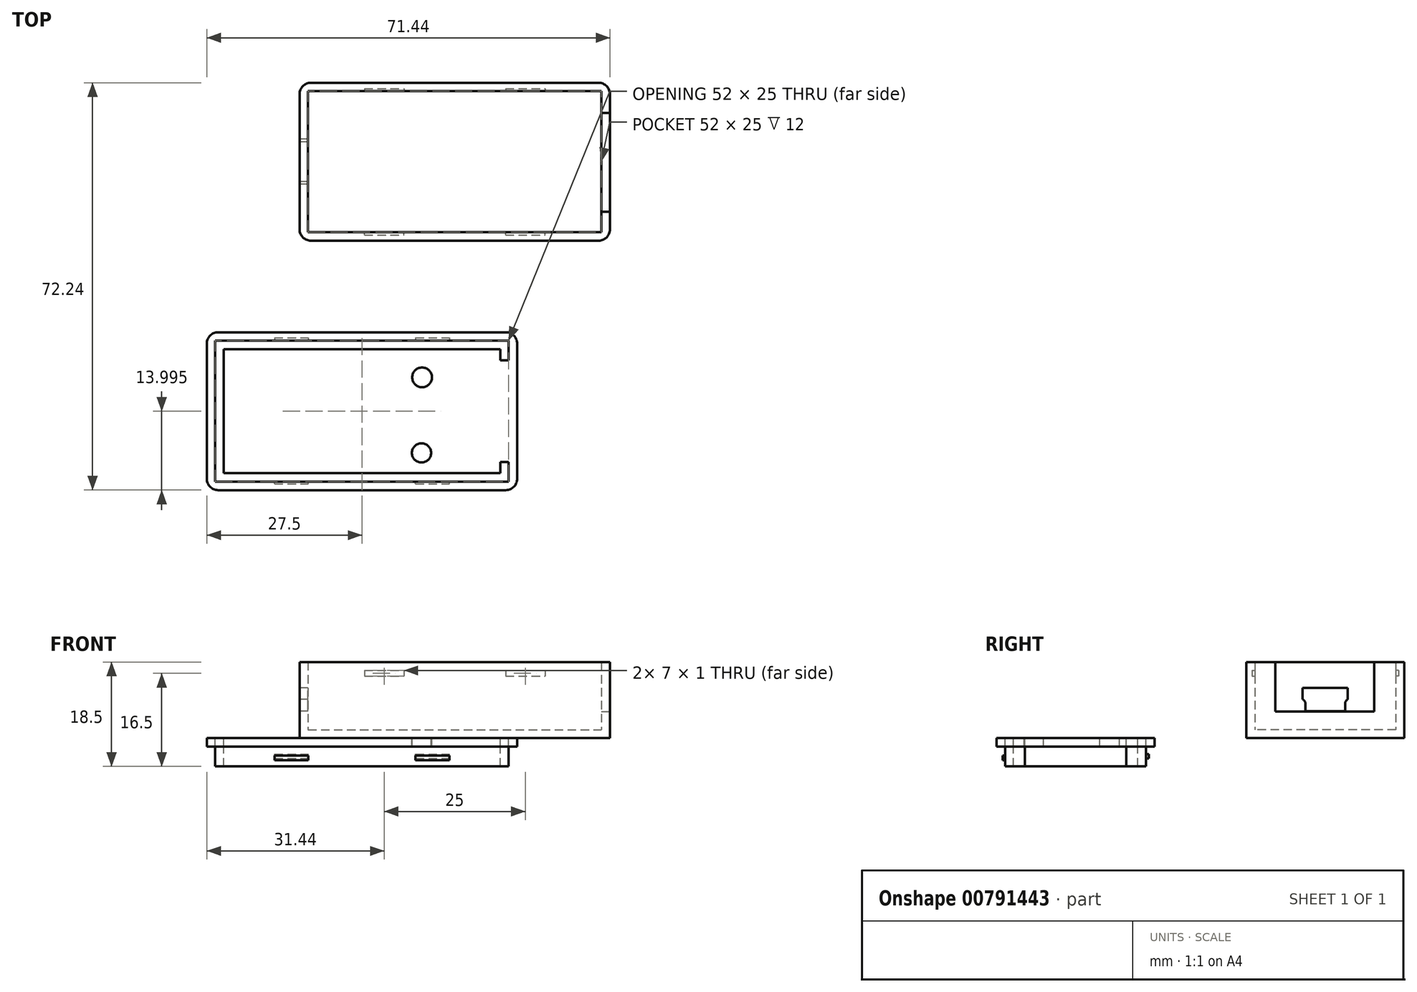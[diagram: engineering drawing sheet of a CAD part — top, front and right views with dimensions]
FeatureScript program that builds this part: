
annotation { "Feature Type Name" : "Feature", "Feature Type Description" : "" }
export const myFeature = defineFeature(function(context is Context, id is Id, definition is map)
    precondition{}
    {
        {
            var Q0;
            Q0=qCreatedBy(makeId("Top.planeOp"),FACE);
            var sketch = newSketch(context, id + "F0", { "sketchPlane" : qUnion([Q0])});
            skLineSegment(sketch, "E0.bottom", {"start": v(-26, 12.5) * mm, "end": v(26, 12.5) * mm});
            skLineSegment(sketch, "E0.top", {"start": v(-26, -12.5) * mm, "end": v(26, -12.5) * mm});
            skLineSegment(sketch, "E0.left", {"start": v(-26, 12.5) * mm, "end": v(-26, -12.5) * mm});
            skLineSegment(sketch, "E0.right", {"start": v(26, 12.5) * mm, "end": v(26, -12.5) * mm});
            skPoint(sketch, "E0.middle", {"position": v(0, 0) * mm});
            skCircle(sketch, "E1", {"center": v(-21.94, 0) * mm, "radius": 1.75 * mm});
            skLineSegment(sketch, "E2.0", {"start": v(-25.5, 14) * mm, "end": v(25.5, 14) * mm});
            skLineSegment(sketch, "E2.1", {"start": v(-27.5, 12) * mm, "end": v(-27.5, -12) * mm});
            skLineSegment(sketch, "E2.2", {"start": v(-25.5, -14) * mm, "end": v(25.5, -14) * mm});
            skLineSegment(sketch, "E2.3", {"start": v(27.5, 12) * mm, "end": v(27.5, -12) * mm});
            skPoint(sketch, "E3.visualSharp", {"position": v(27.5, 14) * mm});
            skArc(sketch, "E3.filletArc", {"start": v(27.5, 12) * mm, "mid": v(26.91, 13.41) * mm, "end": v(25.5, 14) * mm});
            skPoint(sketch, "E4.visualSharp", {"position": v(27.5, -14) * mm});
            skArc(sketch, "E4.filletArc", {"start": v(25.5, -14) * mm, "mid": v(26.91, -13.41) * mm, "end": v(27.5, -12) * mm});
            skPoint(sketch, "E5.visualSharp", {"position": v(-27.5, -14) * mm});
            skArc(sketch, "E5.filletArc", {"start": v(-27.5, -12) * mm, "mid": v(-26.91, -13.41) * mm, "end": v(-25.5, -14) * mm});
            skPoint(sketch, "E6.visualSharp", {"position": v(-27.5, 14) * mm});
            skArc(sketch, "E6.filletArc", {"start": v(-25.5, 14) * mm, "mid": v(-26.91, 13.41) * mm, "end": v(-27.5, 12) * mm});
            skLineSegment(sketch, "E7.bottom", {"start": v(-42.44, -31.74) * mm, "end": v(9.56, -31.74) * mm});
            skLineSegment(sketch, "E7.top", {"start": v(-42.44, -56.74) * mm, "end": v(9.56, -56.74) * mm});
            skLineSegment(sketch, "E7.left", {"start": v(-42.44, -31.74) * mm, "end": v(-42.44, -56.74) * mm});
            skLineSegment(sketch, "E7.right", {"start": v(9.56, -31.74) * mm, "end": v(9.56, -56.74) * mm});
            skPoint(sketch, "E7.middle", {"position": v(-16.44, -44.24) * mm});
            skCircle(sketch, "E8", {"center": v(-38.38, -44.24) * mm, "radius": 1.75 * mm});
            skLineSegment(sketch, "E9.0", {"start": v(-41.94, -30.24) * mm, "end": v(9.06, -30.24) * mm});
            skLineSegment(sketch, "E9.1", {"start": v(-43.94, -32.24) * mm, "end": v(-43.94, -56.24) * mm});
            skLineSegment(sketch, "E9.2", {"start": v(-41.94, -58.24) * mm, "end": v(9.06, -58.24) * mm});
            skLineSegment(sketch, "E9.3", {"start": v(11.06, -32.24) * mm, "end": v(11.06, -56.24) * mm});
            skPoint(sketch, "E10.visualSharp", {"position": v(11.06, -30.24) * mm});
            skArc(sketch, "E10.filletArc", {"start": v(11.06, -32.24) * mm, "mid": v(10.47, -30.83) * mm, "end": v(9.06, -30.24) * mm});
            skPoint(sketch, "E11.visualSharp", {"position": v(11.06, -58.24) * mm});
            skArc(sketch, "E11.filletArc", {"start": v(9.06, -58.24) * mm, "mid": v(10.47, -57.66) * mm, "end": v(11.06, -56.24) * mm});
            skPoint(sketch, "E12.visualSharp", {"position": v(-43.94, -58.24) * mm});
            skArc(sketch, "E12.filletArc", {"start": v(-43.94, -56.24) * mm, "mid": v(-43.35, -57.66) * mm, "end": v(-41.94, -58.24) * mm});
            skPoint(sketch, "E13.visualSharp", {"position": v(-43.94, -30.24) * mm});
            skArc(sketch, "E13.filletArc", {"start": v(-41.94, -30.24) * mm, "mid": v(-43.35, -30.83) * mm, "end": v(-43.94, -32.24) * mm});
            skLineSegment(sketch, "E14.0", {"start": v(-40.94, -33.24) * mm, "end": v(8.06, -33.24) * mm});
            skLineSegment(sketch, "E14.1", {"start": v(-40.94, -33.24) * mm, "end": v(-40.94, -55.24) * mm});
            skLineSegment(sketch, "E14.2", {"start": v(-40.94, -55.24) * mm, "end": v(8.06, -55.24) * mm});
            skLineSegment(sketch, "E14.3", {"start": v(8.06, -33.24) * mm, "end": v(8.06, -55.24) * mm});
            skLineSegment(sketch, "E15", {"start": v(11.06, -35.24) * mm, "end": v(8.06, -35.24) * mm});
            skLineSegment(sketch, "E16", {"start": v(8.06, -53.24) * mm, "end": v(11.06, -53.24) * mm});
            skCircle(sketch, "E17", {"center": v(-5.89, -51.64) * mm, "radius": 1.7 * mm});
            skCircle(sketch, "E18", {"center": v(-5.79, -38.24) * mm, "radius": 1.75 * mm});
            skSolve(sketch);
        }
        {
            var Q0;
            Q0=makeQuery(id+"F0.imprint","IMPRINT",FACE,{"disambiguationData":[TD([[makeQuery(id+"F0.imprint","IMPRINT",EDGE,{"derivedFrom":sQuery(id+"F0.wireOp",EDGE,"E0.bottom")}),-1.0]])]});
            var Q1;
            Q1=makeQuery(id+"F0.imprint","IMPRINT",FACE,{"disambiguationData":[TD([[makeQuery(id+"F0.imprint","IMPRINT",EDGE,{"derivedFrom":sQuery(id+"F0.wireOp",EDGE,"E1")}),1.0]])]});
            extrude(context, id + "F1", {"entities" : qUnion([Q0, Q1]), "depth" : 1.5 * mm, "offsetDistance" : 25 * mm});
        }
        {
            var Q0;
            Q0=makeQuery(id+"F0.imprint","IMPRINT",FACE,{"disambiguationData":[TD([[makeQuery(id+"F0.imprint","IMPRINT",EDGE,{"derivedFrom":sQuery(id+"F0.wireOp",EDGE,"E0.bottom")}),1.0]])]});
            extrude(context, id + "F2", {"entities" : qUnion([Q0]), "operationType" : NewBodyOperationType.ADD, "depth" : 13.5 * mm, "offsetDistance" : 25 * mm});
        }
        {
            var Q0;
            Q0=makeQuery(id+"F2.opExtrude","SWEPT_FACE",FACE,{"disambiguationData":[OSD([sQuery(id+"F0.wireOp",EDGE,"E2.3")])]});
            var sketch = newSketch(context, id + "F3", { "sketchPlane" : qUnion([Q0])});
            skLineSegment(sketch, "E19.bottom", {"start": v(8.65, 13.5) * mm, "end": v(-8.85, 13.5) * mm});
            skLineSegment(sketch, "E19.top", {"start": v(8.65, 4.7) * mm, "end": v(-8.85, 4.7) * mm});
            skLineSegment(sketch, "E19.left", {"start": v(8.65, 13.5) * mm, "end": v(8.65, 4.7) * mm});
            skLineSegment(sketch, "E19.right", {"start": v(-8.85, 13.5) * mm, "end": v(-8.85, 4.7) * mm});
            skSolve(sketch);
        }
        {
            var Q0;
            Q0 = qSketchRegion(id + "F3", true);
            extrude(context, id + "F4", {"entities" : qUnion([Q0]), "operationType" : NewBodyOperationType.REMOVE, "oppositeDirection" : true, "depth" : 25 * mm, "offsetDistance" : 25 * mm});
        }
        {
            var Q0;
            Q0=makeQuery(id+"F2.opExtrude","SWEPT_FACE",FACE,{"disambiguationData":[OSD([sQuery(id+"F0.wireOp",EDGE,"E2.1")])]});
            var sketch = newSketch(context, id + "F5", { "sketchPlane" : qUnion([Q0])});
            skLineSegment(sketch, "E20", {"start": v(0, 13.94) * mm, "end": v(0, 0) * mm, "construction": true});
            skLineSegment(sketch, "E21.bottom", {"start": v(3.5, 6.9) * mm, "end": v(-3.5, 6.9) * mm});
            skLineSegment(sketch, "E21.top", {"start": v(3.5, 4.8) * mm, "end": v(-3.5, 4.8) * mm});
            skLineSegment(sketch, "E21.left", {"start": v(3.5, 6.9) * mm, "end": v(3.5, 4.8) * mm});
            skLineSegment(sketch, "E21.right", {"start": v(-3.5, 6.9) * mm, "end": v(-3.5, 4.8) * mm});
            skLineSegment(sketch, "E22.bottom", {"start": v(4, 8.9) * mm, "end": v(-4, 8.9) * mm});
            skLineSegment(sketch, "E22.top", {"start": v(4, 6.9) * mm, "end": v(-4, 6.9) * mm});
            skLineSegment(sketch, "E22.left", {"start": v(4, 8.9) * mm, "end": v(4, 6.9) * mm});
            skLineSegment(sketch, "E22.right", {"start": v(-4, 8.9) * mm, "end": v(-4, 6.9) * mm});
            skSolve(sketch);
        }
        {
            var Q0;
            Q0=makeQuery(id+"F5.imprint","IMPRINT",FACE,{"disambiguationData":[TD([[makeQuery(id+"F5.imprint","IMPRINT",EDGE,{"derivedFrom":sQuery(id+"F5.wireOp",EDGE,"E21.top")}),-1.0]])]});
            var Q1;
            Q1=makeQuery(id+"F5.imprint","IMPRINT",FACE,{"disambiguationData":[TD([[makeQuery(id+"F5.imprint","IMPRINT",EDGE,{"derivedFrom":sQuery(id+"F5.wireOp",EDGE,"E22.bottom")}),1.0]])]});
            extrude(context, id + "F6", {"entities" : qUnion([Q0, Q1]), "operationType" : NewBodyOperationType.REMOVE, "oppositeDirection" : true, "depth" : 2 * mm, "offsetDistance" : 25 * mm});
        }
        {
            var Q0;
            Q0=makeQuery(id+"F6.boolean.opBoolean","COPY",EDGE,{"derivedFrom":makeQuery(id+"F6.opExtrude","SWEPT_EDGE",EDGE,{"disambiguationData":[OSD([sQuery(id+"F5.wireOp",EDGE,"E21.right"),sQuery(id+"F5.wireOp",EDGE,"E22.top")])]})});
            var Q1;
            Q1=makeQuery(id+"F6.boolean.opBoolean","COPY",EDGE,{"derivedFrom":makeQuery(id+"F6.opExtrude","SWEPT_EDGE",EDGE,{"disambiguationData":[OSD([sQuery(id+"F5.wireOp",EDGE,"E21.left"),sQuery(id+"F5.wireOp",EDGE,"E22.top")])]})});
            fillet(context, id + "F7", {"entities" : qUnion([Q0, Q1]), "radius" : 1 * mm, "tangentPropagation" : true, "allowEdgeOverflow" : false});
        }
        {
            var Q0;
            Q0=makeQuery(id+"F2.opExtrude","SWEPT_FACE",FACE,{"disambiguationData":[OSD([sQuery(id+"F0.wireOp",EDGE,"E0.top")])]});
            var sketch = newSketch(context, id + "F8", { "sketchPlane" : qUnion([Q0])});
            skSolve(sketch);
        }
        {
            var Q0;
            Q0=makeQuery(id+"F2.opExtrude","SWEPT_FACE",FACE,{"disambiguationData":[OSD([sQuery(id+"F0.wireOp",EDGE,"E0.bottom")])]});
            var sketch = newSketch(context, id + "F9", { "sketchPlane" : qUnion([Q0])});
            skLineSegment(sketch, "E23.bottom", {"start": v(-16, 12) * mm, "end": v(-9, 12) * mm});
            skLineSegment(sketch, "E23.top", {"start": v(-16, 11) * mm, "end": v(-9, 11) * mm});
            skLineSegment(sketch, "E23.left", {"start": v(-16, 12) * mm, "end": v(-16, 11) * mm});
            skLineSegment(sketch, "E23.right", {"start": v(-9, 12) * mm, "end": v(-9, 11) * mm});
            skLineSegment(sketch, "E24.1.0.0", {"start": v(16, 12) * mm, "end": v(16, 11) * mm});
            skLineSegment(sketch, "E24.1.0.1", {"start": v(9, 12) * mm, "end": v(16, 12) * mm});
            skLineSegment(sketch, "E24.1.0.2", {"start": v(9, 12) * mm, "end": v(9, 11) * mm});
            skLineSegment(sketch, "E24.1.0.3", {"start": v(9, 11) * mm, "end": v(16, 11) * mm});
            skLineSegment(sketch, "E24.direction1", {"start": v(-9, 11) * mm, "end": v(16, 11) * mm, "construction": true});
            skSolve(sketch);
        }
        {
            var Q0;
            Q0=makeQuery(id+"F9.imprint","IMPRINT",FACE,{"disambiguationData":[TD([[makeQuery(id+"F9.imprint","IMPRINT",EDGE,{"derivedFrom":sQuery(id+"F9.wireOp",EDGE,"E23.bottom")}),-1.0]])]});
            var Q1;
            Q1=makeQuery(id+"F9.imprint","IMPRINT",FACE,{"disambiguationData":[TD([[makeQuery(id+"F9.imprint","IMPRINT",EDGE,{"derivedFrom":sQuery(id+"F9.wireOp",EDGE,"E24.1.0.0")}),-1.0]])]});
            extrude(context, id + "F10", {"entities" : qUnion([Q0, Q1]), "operationType" : NewBodyOperationType.REMOVE, "oppositeDirection" : true, "depth" : 0.5 * mm, "offsetDistance" : 25 * mm});
        }
        {
            var Q0;
            {var subQ0=sQuery(id+"F0.wireOp",EDGE,"E0.top");Q0=makeQuery(id+"F8.imprint","IMPRINT",FACE,{"disambiguationData":[TD([[makeQuery(id+"F8.imprint","IMPRINT",EDGE,{"derivedFrom":makeQuery(id+"F2.opExtrude","CAP_EDGE",EDGE,{"disambiguationData":[OSD([subQ0])],"isStart":false})}),1.0]])]});}
            var sketch = newSketch(context, id + "F11", { "sketchPlane" : qUnion([Q0])});
            skLineSegment(sketch, "E25.bottom", {"start": v(16, 12) * mm, "end": v(9, 12) * mm});
            skLineSegment(sketch, "E25.top", {"start": v(16, 11) * mm, "end": v(9, 11) * mm});
            skLineSegment(sketch, "E25.left", {"start": v(16, 12) * mm, "end": v(16, 11) * mm});
            skLineSegment(sketch, "E25.right", {"start": v(9, 12) * mm, "end": v(9, 11) * mm});
            skLineSegment(sketch, "E26.1.0.0", {"start": v(-9, 11) * mm, "end": v(-16, 11) * mm});
            skLineSegment(sketch, "E26.1.0.1", {"start": v(-9, 12) * mm, "end": v(-16, 12) * mm});
            skLineSegment(sketch, "E26.1.0.2", {"start": v(-16, 12) * mm, "end": v(-16, 11) * mm});
            skLineSegment(sketch, "E26.1.0.3", {"start": v(-9, 12) * mm, "end": v(-9, 11) * mm});
            skLineSegment(sketch, "E26.direction1", {"start": v(9, 11) * mm, "end": v(-16, 11) * mm, "construction": true});
            skSolve(sketch);
        }
        {
            var Q0;
            Q0=makeQuery(id+"F11.imprint","IMPRINT",FACE,{"disambiguationData":[TD([[makeQuery(id+"F11.imprint","IMPRINT",EDGE,{"derivedFrom":sQuery(id+"F11.wireOp",EDGE,"E26.1.0.0")}),-1.0]])]});
            var Q1;
            Q1=makeQuery(id+"F11.imprint","IMPRINT",FACE,{"disambiguationData":[TD([[makeQuery(id+"F11.imprint","IMPRINT",EDGE,{"derivedFrom":sQuery(id+"F11.wireOp",EDGE,"E25.bottom")}),1.0]])]});
            extrude(context, id + "F12", {"entities" : qUnion([Q0, Q1]), "operationType" : NewBodyOperationType.REMOVE, "oppositeDirection" : true, "depth" : 0.5 * mm, "offsetDistance" : 25 * mm});
        }
        {
            var Q0;
            Q0=makeQuery(id+"F0.imprint","IMPRINT",FACE,{"disambiguationData":[TD([[makeQuery(id+"F0.imprint","IMPRINT",EDGE,{"derivedFrom":sQuery(id+"F0.wireOp",EDGE,"E7.bottom")}),1.0]])]});
            var Q1;
            Q1=makeQuery(id+"F0.imprint","IMPRINT",FACE,{"disambiguationData":[TD([[makeQuery(id+"F0.imprint","IMPRINT",EDGE,{"derivedFrom":sQuery(id+"F0.wireOp",EDGE,"E8")}),-1.0]])]});
            var Q2;
            Q2=makeQuery(id+"F0.imprint","IMPRINT",FACE,{"disambiguationData":[TD([[makeQuery(id+"F0.imprint","IMPRINT",EDGE,{"derivedFrom":sQuery(id+"F0.wireOp",EDGE,"E8")}),1.0]])]});
            var Q3;
            {var subQ0=sQuery(id+"F0.wireOp",EDGE,"E15");var subQ1=sQuery(id+"F0.wireOp",EDGE,"E7.right");var subQ2=makeQuery(id+"F0.imprint","INTERSECT",VERTEX,{"derivedFrom":[subQ1,subQ0]});Q3=makeQuery(id+"F0.imprint","IMPRINT",FACE,{"disambiguationData":[TD([[makeQuery(id+"F0.imprint","IMPRINT",EDGE,{"disambiguationData":[TD([[subQ2,-1.0]])],"derivedFrom":subQ1}),-1.0]])]});}
            var Q4;
            {var subQ0=sQuery(id+"F0.wireOp",EDGE,"E15");var subQ1=sQuery(id+"F0.wireOp",EDGE,"E7.right");var subQ2=makeQuery(id+"F0.imprint","INTERSECT",VERTEX,{"derivedFrom":[subQ1,subQ0]});Q4=makeQuery(id+"F0.imprint","IMPRINT",FACE,{"disambiguationData":[TD([[makeQuery(id+"F0.imprint","IMPRINT",EDGE,{"disambiguationData":[TD([[subQ2,-1.0]])],"derivedFrom":subQ1}),1.0]])]});}
            extrude(context, id + "F13", {"entities" : qUnion([Q0, Q1, Q2, Q3, Q4]), "oppositeDirection" : true, "depth" : 1.5 * mm, "offsetDistance" : 25 * mm});
        }
        {
            var Q0;
            Q0=makeQuery(id+"F0.imprint","IMPRINT",FACE,{"disambiguationData":[TD([[makeQuery(id+"F0.imprint","IMPRINT",EDGE,{"derivedFrom":sQuery(id+"F0.wireOp",EDGE,"E7.bottom")}),-1.0]])]});
            extrude(context, id + "F14", {"entities" : qUnion([Q0]), "oppositeDirection" : true, "depth" : 5 * mm, "offsetDistance" : 25 * mm});
        }
        {
            var Q0;
            Q0=makeQuery(id+"F14.opExtrude","SWEPT_FACE",FACE,{"disambiguationData":[OSD([sQuery(id+"F0.wireOp",EDGE,"E7.top")])]});
            var sketch = newSketch(context, id + "F15", { "sketchPlane" : qUnion([Q0])});
            skLineSegment(sketch, "E27.bottom", {"start": v(-31.94, -3.1) * mm, "end": v(-25.94, -3.1) * mm});
            skLineSegment(sketch, "E27.top", {"start": v(-31.94, -3.9) * mm, "end": v(-25.94, -3.9) * mm});
            skLineSegment(sketch, "E27.left", {"start": v(-31.94, -3.1) * mm, "end": v(-31.94, -3.9) * mm});
            skLineSegment(sketch, "E27.right", {"start": v(-25.94, -3.1) * mm, "end": v(-25.94, -3.9) * mm});
            skLineSegment(sketch, "E28.1.0.0", {"start": v(-6.94, -3.1) * mm, "end": v(-0.94, -3.1) * mm});
            skLineSegment(sketch, "E28.1.0.1", {"start": v(-6.94, -3.9) * mm, "end": v(-0.94, -3.9) * mm});
            skLineSegment(sketch, "E28.1.0.2", {"start": v(-0.94, -3.1) * mm, "end": v(-0.94, -3.9) * mm});
            skLineSegment(sketch, "E28.1.0.3", {"start": v(-6.94, -3.1) * mm, "end": v(-6.94, -3.9) * mm});
            skLineSegment(sketch, "E28.direction1", {"start": v(-31.94, -3.1) * mm, "end": v(-6.94, -3.1) * mm, "construction": true});
            skSolve(sketch);
        }
        {
            var Q0;
            Q0=makeQuery(id+"F15.imprint","IMPRINT",FACE,{"disambiguationData":[TD([[makeQuery(id+"F15.imprint","IMPRINT",EDGE,{"derivedFrom":sQuery(id+"F15.wireOp",EDGE,"E27.bottom")}),-1.0]])]});
            var Q1;
            Q1=makeQuery(id+"F15.imprint","IMPRINT",FACE,{"disambiguationData":[TD([[makeQuery(id+"F15.imprint","IMPRINT",EDGE,{"derivedFrom":sQuery(id+"F15.wireOp",EDGE,"E28.1.0.0")}),-1.0]])]});
            extrude(context, id + "F16", {"entities" : qUnion([Q0, Q1]), "operationType" : NewBodyOperationType.ADD, "depth" : 0.4 * mm, "offsetDistance" : 25 * mm});
        }
        {
            var Q0;
            Q0=makeQuery(id+"F14.opExtrude","SWEPT_FACE",FACE,{"disambiguationData":[OSD([sQuery(id+"F0.wireOp",EDGE,"E7.bottom")])]});
            var sketch = newSketch(context, id + "F17", { "sketchPlane" : qUnion([Q0])});
            skLineSegment(sketch, "E29.bottom", {"start": v(31.94, -3.6) * mm, "end": v(25.94, -3.6) * mm});
            skLineSegment(sketch, "E29.top", {"start": v(31.94, -2.8) * mm, "end": v(25.94, -2.8) * mm});
            skLineSegment(sketch, "E29.left", {"start": v(31.94, -3.6) * mm, "end": v(31.94, -2.8) * mm});
            skLineSegment(sketch, "E29.right", {"start": v(25.94, -3.6) * mm, "end": v(25.94, -2.8) * mm});
            skLineSegment(sketch, "E30.1.0.0", {"start": v(6.94, -3.6) * mm, "end": v(0.94, -3.6) * mm});
            skLineSegment(sketch, "E30.1.0.1", {"start": v(6.94, -2.8) * mm, "end": v(0.94, -2.8) * mm});
            skLineSegment(sketch, "E30.1.0.2", {"start": v(6.94, -3.6) * mm, "end": v(6.94, -2.8) * mm});
            skLineSegment(sketch, "E30.1.0.3", {"start": v(0.94, -3.6) * mm, "end": v(0.94, -2.8) * mm});
            skLineSegment(sketch, "E30.direction1", {"start": v(25.94, -3.6) * mm, "end": v(0.94, -3.6) * mm, "construction": true});
            skSolve(sketch);
        }
        {
            var Q0;
            Q0=makeQuery(id+"F17.imprint","IMPRINT",FACE,{"disambiguationData":[TD([[makeQuery(id+"F17.imprint","IMPRINT",EDGE,{"derivedFrom":sQuery(id+"F17.wireOp",EDGE,"E29.bottom")}),-1.0]])]});
            var Q1;
            Q1=makeQuery(id+"F17.imprint","IMPRINT",FACE,{"disambiguationData":[TD([[makeQuery(id+"F17.imprint","IMPRINT",EDGE,{"derivedFrom":sQuery(id+"F17.wireOp",EDGE,"E30.1.0.0")}),-1.0]])]});
            extrude(context, id + "F18", {"entities" : qUnion([Q0, Q1]), "operationType" : NewBodyOperationType.ADD, "depth" : 0.5 * mm, "offsetDistance" : 25 * mm});
        }
    });
